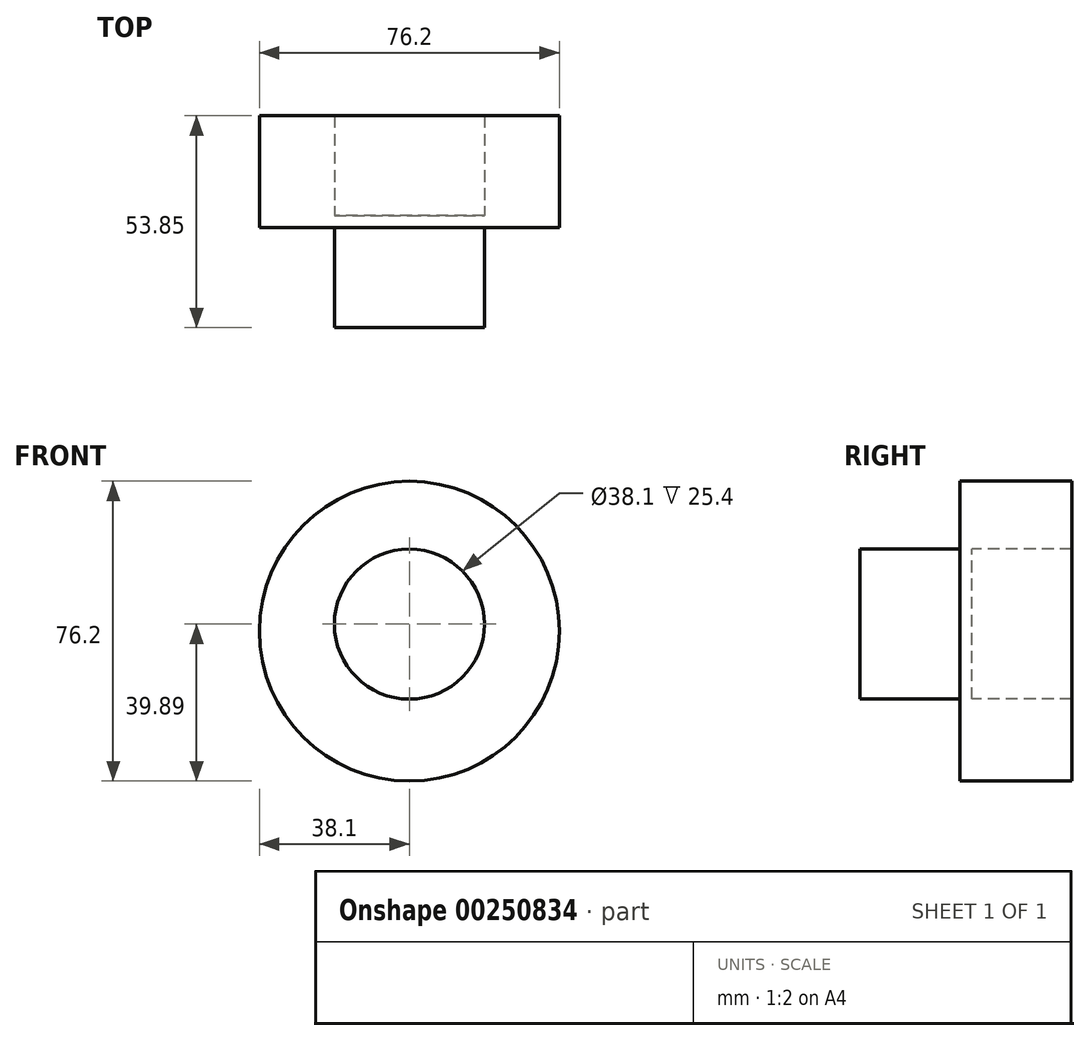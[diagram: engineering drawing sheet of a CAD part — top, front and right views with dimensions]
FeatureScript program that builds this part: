
annotation { "Feature Type Name" : "Feature", "Feature Type Description" : "" }
export const myFeature = defineFeature(function(context is Context, id is Id, definition is map)
    precondition{}
    {
        {
            var Q0;
            Q0=qCreatedBy(makeId("Front.planeOp"),FACE);
            var sketch = newSketch(context, id + "F0", { "sketchPlane" : qUnion([Q0])});
            skCircle(sketch, "E0", {"center": v(0, -1.79) * mm, "radius": 38.1 * mm});
            skCircle(sketch, "E1", {"center": v(0, 0) * mm, "radius": 19.05 * mm});
            skSolve(sketch);
        }
        {
            var Q0;
            Q0=makeQuery(id+"F0.imprint","IMPRINT",FACE,{"disambiguationData":[TD([[makeQuery(id+"F0.imprint","IMPRINT",EDGE,{"derivedFrom":sQuery(id+"F0.wireOp",EDGE,"E1")}),1.0]])]});
            extrude(context, id + "F1", {"entities" : qUnion([Q0]), "depth" : 25.4 * mm});
        }
        {
            var Q0;
            Q0=makeQuery(id+"F0.imprint","IMPRINT",FACE,{"disambiguationData":[TD([[makeQuery(id+"F0.imprint","IMPRINT",EDGE,{"derivedFrom":sQuery(id+"F0.wireOp",EDGE,"E0")}),1.0]])]});
            var Q1;
            Q1=makeQuery(id+"F1.opExtrude","CAP_FACE",FACE,{"disambiguationData":[OSD([sQuery(id+"F0.wireOp",EDGE,"E1")])],"isStart":false});
            extrude(context, id + "F2", {"entities" : qUnion([Q0, Q1]), "operationType" : NewBodyOperationType.ADD, "oppositeDirection" : true, "depth" : 28.45 * mm});
        }
    });
